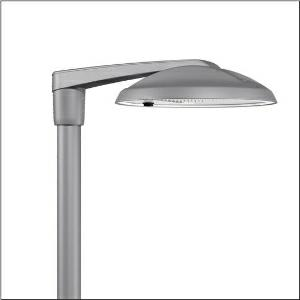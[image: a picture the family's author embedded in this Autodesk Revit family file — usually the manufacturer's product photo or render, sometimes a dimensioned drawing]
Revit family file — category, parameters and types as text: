
# Revit family: dl_r__50_iq_mini___st1_0a_5xa248d31u08me_8dcd
name_source: partatom
category: Lighting Fixtures
units: mm (PartAtom-declared; Revit-internal decimal feet)

## family parameters
Cut with Voids When Loaded = No
Host = Face
Light Source = No
Part Type = Normal
Room Calculation Point = No
Round Connector Dimension = Use Diameter
Shared = No

## types (1)
- --- (1 x LED, 15720 lm, 107 W, 3000K)
    Apparent Load = 107 VA
    CIE Flux Codes = 37 72 97 100 100
    Color Rendering = 70
    Color Temperature = 3000K
    Default Elevation = 1800 mm
    Description = DL® 50 iQ mini, mast luminaire, primary light control with lens, of PMMA, primary optical cover: cover, of toughened safety glass, transparent, light distribution: ST1.0a, light emission: direct distribution, primary light characteristic: asymmetric, installation type: post-top, side-entry, LED, High Power LED, rated luminous flux: 15.720lm, luminous efficacy: 147lm/W, light colour: 730, colour temperature: 3000K, control gear: iQ-Street Remote, D4i with power reduction, control: optimised constant luminous flux control (CLO 2.0), Desk-Remote (wireless, voltage-free reading and setting of iQ features in the workshop via application-optimized NFC function/RFID function), Light-Fading, Smart-Wire, Night-Set, Lumen-Switch, Temp-Guard, Auto-Match, Street-Remote, pre-setting: logarithmic dimming characteristic, mains connection: 220..240V, AC, 50/60Hz, connection cable pre-assembled, cable length: 10,5m, start of lifetime: 107W, end of service life: 113W, reduction: 47W, luminaire housing, of diecast aluminium, powder-coated, Siteco® metallic grey (DB 702S), inclination adjustable: 0°, 5°, 10° (post-top) | 0°, -5°, -10°, -15° (side-entry), please order mast post-top element or mast side-entry element separately, diameter: 500mm, height: 115mm, post-top: for spigot size d x l = 76 x 100mm; with reducer (optional accessory) 60 x 100mm | side-entry: for spigot size d x l = 60 x 100mm; with reducer (optional accessory) 42 x 100mm, mounting height: 4..6m, Smart Interface below, protection rating (complete): IP66, insulation class (complete): insulation class II (safety insulation), certification: CE, ENEC, ENEC+, VDE, impact resistance: IK08, permissible operating ambient temperature for outdoor applications: -25..+40°C, standard-compliant lighting for roads and squares, packaging unit: 1 piece

Light Distribution: ST1.0a
    Height = 115 mm
    Lamp = 1 x LED
    Lamp Light Flux = 15720 lm
    Lamp Power = 107 W
    Lamp count = 1
    Length = 500 mm
    Luminous efficacy = 147 lm/W
    Manufacturer = Siteco
    ModVariant = No
    Model = 5XA248D31U08ME
    Number of Poles = 1
    OnlyDefault = Yes
    Power Factor = 1
    Product Name = DL® 50 iQ mini | ST1.0a
    Product group = mast luminaire | pylon top
    ProductGroupID = 6100
    Protection Class = Protection class II
    Protection Degree = IP 66
    RLX_Detail_Level = 1
    RLX_Emergency_Light_Flux = 0 lm
    RLX_Emergency_Type = 0
    RLX_Emergency_Type_DB = No
    RlxData = <blob elided: 106349 chars, md5=08442e87>
    Socket = socket
    Standby Power = 0 W
    System Light Flux = 15720 lm
    System Power = 107 W
    Type Comments = factory setting: luminous flux: 100 % | dim-lin: 254 | 565 mA
    Type Image = l_1296955.jpg
    URL = http://relux.com
    VarID = @adj_065812
    Voltage = 0 V
    Weight = 0.00 kg
    Width = 0 mm  [stored 0 ft]

note: [stored X ft] marks values corroborated as IEEE doubles in the binary element streams (Revit-internal decimal feet)

## geometry (parser evidence)
native form markers: Blend x4, Sweep x9
no freeform markers — native parametric forms only
